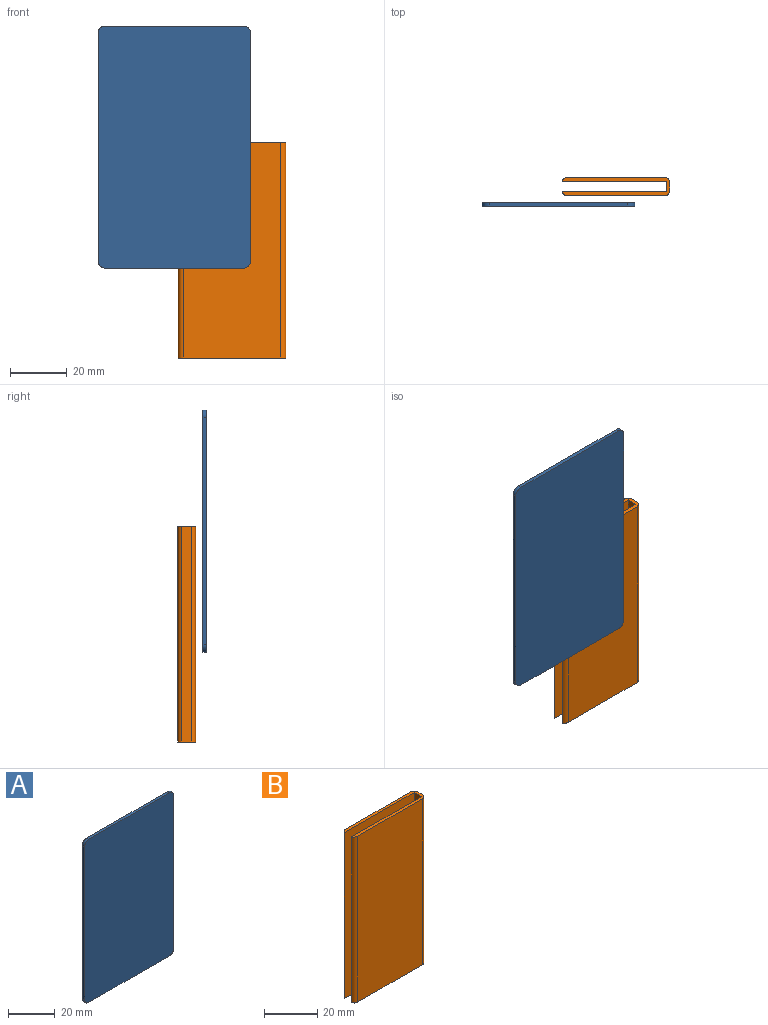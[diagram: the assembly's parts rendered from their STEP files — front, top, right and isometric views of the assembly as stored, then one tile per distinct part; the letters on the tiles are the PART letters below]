
ASSEMBLY  parts=2 mates=1
PART A: 10 faces, bbox 54x1.3x85.6 mm
  f0: plane 80.52x1.27mm, normal (1,0,0), area 102.3mm2, adj f4,f5,f6,f9
  f1: plane 48.9x1.27mm, normal (0,0,1), area 62.1mm2, adj f4,f5,f6,f7
  f2: plane 80.52x1.27mm, normal (-1,0,0), area 102.3mm2, adj f4,f5,f7,f8
  f3: plane 48.9x1.27mm, normal (0,0,-1), area 62.1mm2, adj f4,f5,f8,f9
  f4: plane 85.6x53.98mm, normal (0,-1,0), area 4614.6mm2, adj f0,f1,f2,f3,f6,f7,f8,f9
  f5: plane 85.6x53.98mm, normal (0,1,0), area 4614.6mm2, adj f0,f1,f2,f3,f6,f7,f8,f9
  f6: cylinder r=2.54mm len=2.54mm, axis (0,1,0), area 5.1mm2, adj f0,f1,f4,f5
  f7: cylinder r=2.54mm len=2.54mm, axis (0,-1,0), area 5.1mm2, adj f1,f2,f4,f5
  f8: cylinder r=2.54mm len=2.54mm, axis (0,1,0), area 5.1mm2, adj f2,f3,f4,f5
  f9: cylinder r=2.54mm len=2.54mm, axis (0,-1,0), area 5.1mm2, adj f0,f3,f4,f5
PART B: 12 faces, bbox 38.1x6.4x76.2 mm
  f0: plane 76.2x2.54mm, normal (1,0,0), area 193.5mm2, adj f6,f7,f8,f11
  f1: plane 76.2x34.4mm, normal (0,1,0), area 2621.2mm2, adj f6,f7,f8,f9
  f2: plane 76.2x36.83mm, normal (0,-1,0), area 2806.4mm2, adj f3,f6,f7,f9
  f3: plane 76.2x3.81mm, normal (-1,0,0), area 290.3mm2, adj f2,f4,f6,f7
  f4: plane 76.2x36.83mm, normal (0,1,0), area 2806.4mm2, adj f3,f6,f7,f10
  f5: plane 76.2x34.4mm, normal (0,-1,0), area 2621.2mm2, adj f6,f7,f10,f11
  f6: plane 38.1x6.35mm, normal (0,0,1), area 98.8mm2, adj f0,f1,f2,f3,f4,f5,f8,f9
  f7: plane 38.1x6.35mm, normal (0,0,-1), area 98.8mm2, adj f0,f1,f2,f3,f4,f5,f8,f9
  f8: cylinder r=1.91mm len=76.2mm, axis (0,0,-1), area 228mm2, adj f0,f1,f6,f7
  f9: cylinder r=1.91mm len=76.2mm, axis (0,0,-1), area 178.7mm2, adj f1,f2,f6,f7
  f10: cylinder r=1.91mm len=76.2mm, axis (0,0,-1), area 178.7mm2, adj f4,f5,f6,f7
  f11: cylinder r=1.91mm len=76.2mm, axis (0,0,1), area 228mm2, adj f0,f5,f6,f7
PLACE A t=(-53.79,-23.53,41.74)mm
PLACE B t=(-33.42,-17.8,-32.85)mm
MATE parallel A.f5 <-> B.f2  axis (0,1,0) through (-53.79,-23.53,41.74)mm
